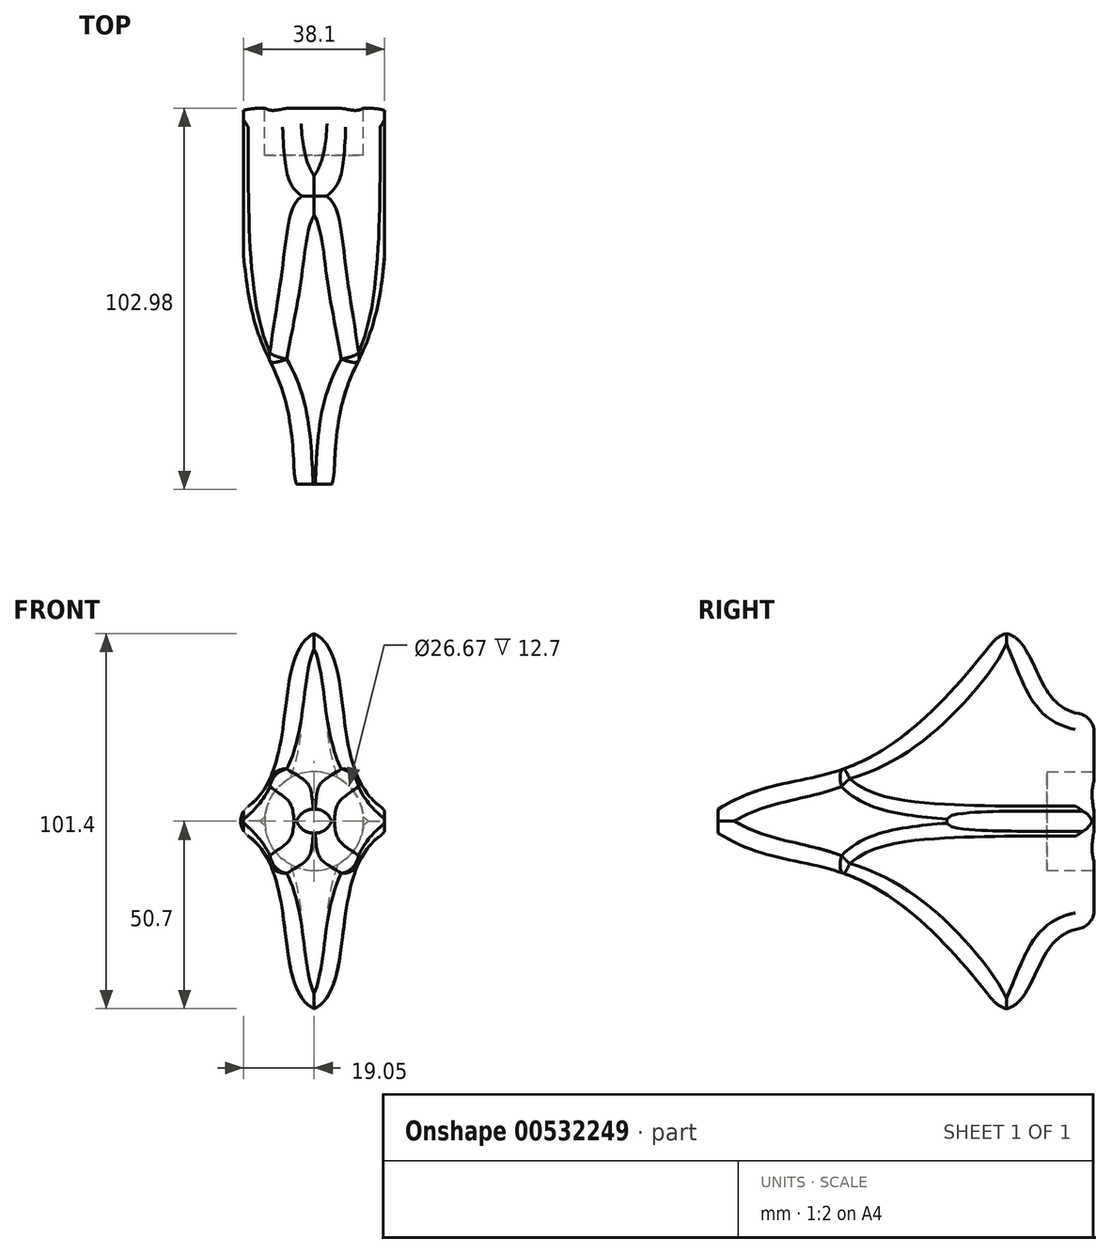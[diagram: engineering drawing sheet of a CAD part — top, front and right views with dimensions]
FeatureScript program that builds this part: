
annotation { "Feature Type Name" : "Feature", "Feature Type Description" : "" }
export const myFeature = defineFeature(function(context is Context, id is Id, definition is map)
    precondition{}
    {
        {
            var Q0;
            Q0=qCreatedBy(makeId("Front.planeOp"),FACE);
            var sketch = newSketch(context, id + "F0", { "sketchPlane" : qUnion([Q0])});
            skLineSegment(sketch, "E0.bottom", {"start": v(-16, 59.8) * mm, "end": v(22.1, 59.8) * mm});
            skLineSegment(sketch, "E0.top", {"start": v(-16, -41.8) * mm, "end": v(22.1, -41.8) * mm});
            skLineSegment(sketch, "E0.left", {"start": v(-16, 59.8) * mm, "end": v(-16, -41.8) * mm});
            skLineSegment(sketch, "E0.right", {"start": v(22.1, 59.8) * mm, "end": v(22.1, -41.8) * mm});
            skLineSegment(sketch, "E1", {"start": v(3.06, 59.8) * mm, "end": v(3.06, -41.8) * mm, "construction": true});
            skLineSegment(sketch, "E2", {"start": v(22.1, 9) * mm, "end": v(-16, 9) * mm, "construction": true});
            skFitSpline(sketch, "E3", {"points": [v(3.06, 59.8) * mm, v(-16, 12.22) * mm], "startDerivative": vector(-36.11, -18.07) * mm, "endDerivative": vector(-47.97, -28.44) * mm});
            skFitSpline(sketch, "E4.MirrorCS", {"points": [v(3.06, 59.8) * mm, v(22.1, 12.22) * mm], "startDerivative": vector(36.11, -18.07) * mm, "endDerivative": vector(47.97, -28.44) * mm});
            skFitSpline(sketch, "E5.MirrorCS", {"points": [v(3.06, -41.8) * mm, v(22.1, 5.78) * mm], "startDerivative": vector(36.11, 18.07) * mm, "endDerivative": vector(47.97, 28.44) * mm});
            skFitSpline(sketch, "E6.MirrorCS", {"points": [v(3.06, -41.8) * mm, v(-16, 5.78) * mm], "startDerivative": vector(-36.11, 18.07) * mm, "endDerivative": vector(-47.97, 28.44) * mm});
            skCircle(sketch, "E7", {"center": v(3.06, 9) * mm, "radius": 13.34 * mm});
            skSolve(sketch);
        }
        {
            var Q0;
            {var subQ3=sQuery(id+"F0.wireOp",EDGE,"E3");Q0=makeQuery(id+"F0.imprint","IMPRINT",FACE,{"disambiguationData":[TD([[makeQuery(id+"F0.imprint","IMPRINT",EDGE,{"derivedFrom":subQ3}),1.0]])]});}
            var Q1;
            Q1=makeQuery(id+"F0.imprint","IMPRINT",FACE,{"disambiguationData":[TD([[makeQuery(id+"F0.imprint","IMPRINT",EDGE,{"derivedFrom":sQuery(id+"F0.wireOp",EDGE,"kdTat6LL-pgFr-9cCU-HG4Y-xFUNoQWsQAuV")}),1.0]])]});
            var Q2;
            Q2=makeQuery(id+"F0.imprint","IMPRINT",FACE,{"disambiguationData":[TD([[makeQuery(id+"F0.imprint","IMPRINT",EDGE,{"derivedFrom":sQuery(id+"F0.wireOp",EDGE,"E7")}),1.0]])]});
            extrude(context, id + "F1", {"entities" : qUnion([Q0, Q1, Q2]), "depth" : 101.6 * mm, "offsetDistance" : 25.4 * mm});
        }
        {
            var Q0;
            Q0=makeQuery(id+"F0.imprint","IMPRINT",FACE,{"disambiguationData":[TD([[makeQuery(id+"F0.imprint","IMPRINT",EDGE,{"derivedFrom":sQuery(id+"F0.wireOp",EDGE,"E7")}),1.0]])]});
            extrude(context, id + "F2", {"entities" : qUnion([Q0]), "operationType" : NewBodyOperationType.REMOVE, "depth" : 12.7 * mm, "offsetDistance" : 25.4 * mm});
        }
        {
            var Q0;
            Q0=makeQuery(id+"F1.opExtrude","SWEPT_FACE",FACE,{"disambiguationData":[OSD([sQuery(id+"F0.wireOp",EDGE,"E0.left")])]});
            var sketch = newSketch(context, id + "F3", { "sketchPlane" : qUnion([Q0])});
            skFitSpline(sketch, "E8", {"points": [v(101.6, 12.22) * mm, v(24.43, 61.45) * mm], "startDerivative": vector(-72.72, 45.7) * mm, "endDerivative": vector(-116.16, 157.36) * mm});
            skLineSegment(sketch, "E9", {"start": v(101.6, 9) * mm, "end": v(0, 9) * mm, "construction": true});
            skFitSpline(sketch, "E10.MirrorCS", {"points": [v(101.6, 5.78) * mm, v(24.43, -43.45) * mm], "startDerivative": vector(-72.72, -45.7) * mm, "endDerivative": vector(-116.16, -157.36) * mm});
            skLineSegment(sketch, "E11", {"start": v(24.43, 61.45) * mm, "end": v(105.94, 61.45) * mm});
            skLineSegment(sketch, "E12", {"start": v(105.94, 61.45) * mm, "end": v(101.6, 12.22) * mm});
            skLineSegment(sketch, "E13.MirrorCS", {"start": v(24.43, -43.45) * mm, "end": v(105.94, -43.45) * mm});
            skLineSegment(sketch, "E14.MirrorCS", {"start": v(105.94, -43.45) * mm, "end": v(101.6, 5.78) * mm});
            skFitSpline(sketch, "E15", {"points": [v(24.43, 61.45) * mm, v(-2.72, 38.08) * mm], "startDerivative": vector(-35.2, -20.24) * mm, "endDerivative": vector(-59.28, 8.68) * mm});
            skLineSegment(sketch, "E16", {"start": v(24.43, 61.45) * mm, "end": v(-20.32, 72.54) * mm});
            skLineSegment(sketch, "E17", {"start": v(-20.32, 72.54) * mm, "end": v(-2.72, 38.08) * mm});
            skLineSegment(sketch, "E18.MirrorCS", {"start": v(-20.32, -54.54) * mm, "end": v(-2.72, -20.08) * mm});
            skFitSpline(sketch, "E19.MirrorCS", {"points": [v(24.43, -43.45) * mm, v(-2.72, -20.08) * mm], "startDerivative": vector(-35.2, 20.24) * mm, "endDerivative": vector(-59.28, -8.68) * mm});
            skLineSegment(sketch, "E20.MirrorCS", {"start": v(24.43, -43.45) * mm, "end": v(-20.32, -54.54) * mm});
            skSolve(sketch);
        }
        {
            var Q0;
            Q0=makeQuery(id+"F3.imprint","IMPRINT",FACE,{"disambiguationData":[TD([[makeQuery(id+"F3.imprint","IMPRINT",EDGE,{"derivedFrom":sQuery(id+"F3.wireOp",EDGE,"E8")}),-1.0]])]});
            var Q1;
            Q1=makeQuery(id+"F3.imprint","IMPRINT",FACE,{"disambiguationData":[TD([[makeQuery(id+"F3.imprint","IMPRINT",EDGE,{"derivedFrom":sQuery(id+"F3.wireOp",EDGE,"E10.MirrorCS")}),1.0]])]});
            extrude(context, id + "F4", {"entities" : qUnion([Q0, Q1]), "operationType" : NewBodyOperationType.REMOVE, "oppositeDirection" : true, "depth" : 762 * mm, "offsetDistance" : 25.4 * mm});
        }
        {
            var Q0;
            Q0=qCreatedBy(makeId("Top.planeOp"),FACE);
            var sketch = newSketch(context, id + "F5", { "sketchPlane" : qUnion([Q0])});
            skLineSegment(sketch, "E21", {"start": v(3.06, -117.6) * mm, "end": v(3.06, -54.23) * mm, "construction": true});
            skLineSegment(sketch, "E22", {"start": v(-16.83, -16.27) * mm, "end": v(-16.83, -108.32) * mm});
            skLineSegment(sketch, "E23", {"start": v(-16.83, -108.32) * mm, "end": v(3.06, -101.56) * mm});
            skLineSegment(sketch, "E24.MirrorCS", {"start": v(22.95, -16.27) * mm, "end": v(22.95, -108.32) * mm});
            skLineSegment(sketch, "E25.MirrorCS", {"start": v(22.95, -108.32) * mm, "end": v(3.06, -101.56) * mm});
            skFitSpline(sketch, "E26", {"points": [v(-16.83, -16.27) * mm, v(-2.27, -103.37) * mm], "startDerivative": vector(0, -195.22) * mm, "endDerivative": vector(0.96, -140.8) * mm});
            skFitSpline(sketch, "E27.MirrorCS", {"points": [v(22.95, -16.27) * mm, v(8.39, -103.37) * mm], "startDerivative": vector(0, -195.22) * mm, "endDerivative": vector(-0.96, -140.8) * mm});
            skSolve(sketch);
        }
        {
            var Q0;
            {var subQ0=sQuery(id+"F5.wireOp",EDGE,"E22");Q0=makeQuery(id+"F5.imprint","IMPRINT",FACE,{"disambiguationData":[TD([[makeQuery(id+"F5.imprint","IMPRINT",EDGE,{"derivedFrom":subQ0}),1.0]])]});}
            var Q1;
            {var subQ0=sQuery(id+"F5.wireOp",EDGE,"E24.MirrorCS");Q1=makeQuery(id+"F5.imprint","IMPRINT",FACE,{"disambiguationData":[TD([[makeQuery(id+"F5.imprint","IMPRINT",EDGE,{"derivedFrom":subQ0}),-1.0]])]});}
            extrude(context, id + "F6", {"entities" : qUnion([Q0, Q1]), "operationType" : NewBodyOperationType.REMOVE, "endBound" : BoundingType.SYMMETRIC, "oppositeDirection" : true, "depth" : 762 * mm, "offsetDistance" : 25.4 * mm});
        }
        {
            var Q0;
            Q0=makeQuery(id+"F3.imprint","IMPRINT",FACE,{"disambiguationData":[TD([[makeQuery(id+"F3.imprint","IMPRINT",EDGE,{"derivedFrom":sQuery(id+"F3.wireOp",EDGE,"E15")}),-1.0]])]});
            var Q1;
            Q1=makeQuery(id+"F3.imprint","IMPRINT",FACE,{"disambiguationData":[TD([[makeQuery(id+"F3.imprint","IMPRINT",EDGE,{"derivedFrom":sQuery(id+"F3.wireOp",EDGE,"E18.MirrorCS")}),-1.0]])]});
            extrude(context, id + "F7", {"entities" : qUnion([Q0, Q1]), "operationType" : NewBodyOperationType.REMOVE, "oppositeDirection" : true, "depth" : 50.8 * mm, "offsetDistance" : 25.4 * mm});
        }
        {
            var Q0;
            Q0=makeQuery(id+"F6.boolean.opBoolean","INTERSECT",EDGE,{"derivedFrom":[makeQuery(id+"F4.boolean.opBoolean","COPY",FACE,{"derivedFrom":makeQuery(id+"F4.opExtrude","SWEPT_FACE",FACE,{"disambiguationData":[OSD([sQuery(id+"F3.wireOp",EDGE,"E10.MirrorCS")])]})}),makeQuery(id+"F6.opExtrude","SWEPT_FACE",FACE,{"disambiguationData":[OSD([sQuery(id+"F5.wireOp",EDGE,"E26")])]})]});
            var Q1;
            Q1=makeQuery(id+"F6.boolean.opBoolean","INTERSECT",EDGE,{"derivedFrom":[makeQuery(id+"F4.boolean.opBoolean","COPY",FACE,{"derivedFrom":makeQuery(id+"F4.opExtrude","SWEPT_FACE",FACE,{"disambiguationData":[OSD([sQuery(id+"F3.wireOp",EDGE,"E8")])]})}),makeQuery(id+"F6.opExtrude","SWEPT_FACE",FACE,{"disambiguationData":[OSD([sQuery(id+"F5.wireOp",EDGE,"E26")])]})]});
            var Q2;
            Q2=makeQuery(id+"F6.boolean.opBoolean","INTERSECT",EDGE,{"derivedFrom":[makeQuery(id+"F4.boolean.opBoolean","COPY",FACE,{"derivedFrom":makeQuery(id+"F4.opExtrude","SWEPT_FACE",FACE,{"disambiguationData":[OSD([sQuery(id+"F3.wireOp",EDGE,"E10.MirrorCS")])]})}),makeQuery(id+"F6.opExtrude","SWEPT_FACE",FACE,{"disambiguationData":[OSD([sQuery(id+"F5.wireOp",EDGE,"E27.MirrorCS")])]})]});
            var Q3;
            Q3=makeQuery(id+"F6.boolean.opBoolean","INTERSECT",EDGE,{"derivedFrom":[makeQuery(id+"F4.boolean.opBoolean","COPY",FACE,{"derivedFrom":makeQuery(id+"F4.opExtrude","SWEPT_FACE",FACE,{"disambiguationData":[OSD([sQuery(id+"F3.wireOp",EDGE,"E8")])]})}),makeQuery(id+"F6.opExtrude","SWEPT_FACE",FACE,{"disambiguationData":[OSD([sQuery(id+"F5.wireOp",EDGE,"E27.MirrorCS")])]})]});
            var Q4;
            Q4=makeQuery(id+"F4.boolean.opBoolean","INTERSECT",EDGE,{"derivedFrom":[makeQuery(id+"F1.opExtrude","SWEPT_FACE",FACE,{"disambiguationData":[OSD([sQuery(id+"F0.wireOp",EDGE,"E6.MirrorCS")])]}),makeQuery(id+"F4.opExtrude","SWEPT_FACE",FACE,{"disambiguationData":[OSD([sQuery(id+"F3.wireOp",EDGE,"E10.MirrorCS")])]})]});
            var Q5;
            Q5=makeQuery(id+"F4.boolean.opBoolean","INTERSECT",EDGE,{"derivedFrom":[makeQuery(id+"F1.opExtrude","SWEPT_FACE",FACE,{"disambiguationData":[OSD([sQuery(id+"F0.wireOp",EDGE,"E5.MirrorCS")])]}),makeQuery(id+"F4.opExtrude","SWEPT_FACE",FACE,{"disambiguationData":[OSD([sQuery(id+"F3.wireOp",EDGE,"E10.MirrorCS")])]})]});
            var Q6;
            Q6=makeQuery(id+"F6.boolean.opBoolean","INTERSECT",EDGE,{"derivedFrom":[makeQuery(id+"F1.opExtrude","SWEPT_FACE",FACE,{"disambiguationData":[OSD([sQuery(id+"F0.wireOp",EDGE,"E5.MirrorCS")])]}),makeQuery(id+"F6.opExtrude","SWEPT_FACE",FACE,{"disambiguationData":[OSD([sQuery(id+"F5.wireOp",EDGE,"E27.MirrorCS")])]})]});
            var Q7;
            Q7=makeQuery(id+"F6.boolean.opBoolean","INTERSECT",EDGE,{"derivedFrom":[makeQuery(id+"F1.opExtrude","SWEPT_FACE",FACE,{"disambiguationData":[OSD([sQuery(id+"F0.wireOp",EDGE,"E4.MirrorCS")])]}),makeQuery(id+"F6.opExtrude","SWEPT_FACE",FACE,{"disambiguationData":[OSD([sQuery(id+"F5.wireOp",EDGE,"E27.MirrorCS")])]})]});
            var Q8;
            Q8=makeQuery(id+"F4.boolean.opBoolean","INTERSECT",EDGE,{"derivedFrom":[makeQuery(id+"F1.opExtrude","SWEPT_FACE",FACE,{"disambiguationData":[OSD([sQuery(id+"F0.wireOp",EDGE,"E4.MirrorCS")])]}),makeQuery(id+"F4.opExtrude","SWEPT_FACE",FACE,{"disambiguationData":[OSD([sQuery(id+"F3.wireOp",EDGE,"E8")])]})]});
            var Q9;
            Q9=makeQuery(id+"F4.boolean.opBoolean","INTERSECT",EDGE,{"derivedFrom":[makeQuery(id+"F1.opExtrude","SWEPT_FACE",FACE,{"disambiguationData":[OSD([sQuery(id+"F0.wireOp",EDGE,"E3")])]}),makeQuery(id+"F4.opExtrude","SWEPT_FACE",FACE,{"disambiguationData":[OSD([sQuery(id+"F3.wireOp",EDGE,"E8")])]})]});
            var Q10;
            Q10=makeQuery(id+"F6.boolean.opBoolean","INTERSECT",EDGE,{"derivedFrom":[makeQuery(id+"F1.opExtrude","SWEPT_FACE",FACE,{"disambiguationData":[OSD([sQuery(id+"F0.wireOp",EDGE,"E3")])]}),makeQuery(id+"F6.opExtrude","SWEPT_FACE",FACE,{"disambiguationData":[OSD([sQuery(id+"F5.wireOp",EDGE,"E26")])]})]});
            var Q11;
            Q11=makeQuery(id+"F6.boolean.opBoolean","INTERSECT",EDGE,{"derivedFrom":[makeQuery(id+"F1.opExtrude","SWEPT_FACE",FACE,{"disambiguationData":[OSD([sQuery(id+"F0.wireOp",EDGE,"E6.MirrorCS")])]}),makeQuery(id+"F6.opExtrude","SWEPT_FACE",FACE,{"disambiguationData":[OSD([sQuery(id+"F5.wireOp",EDGE,"E26")])]})]});
            fillet(context, id + "F8", {"entities" : qUnion([Q0, Q1, Q2, Q3, Q4, Q5, Q6, Q7, Q8, Q9, Q10, Q11]), "radius" : 5.08 * mm, "tangentPropagation" : true, "allowEdgeOverflow" : false});
        }
        {
            var Q0;
            Q0=makeQuery(id+"F7.boolean.opBoolean","INTERSECT",EDGE,{"derivedFrom":[makeQuery(id+"F1.opExtrude","SWEPT_FACE",FACE,{"disambiguationData":[OSD([sQuery(id+"F0.wireOp",EDGE,"E3")])]}),makeQuery(id+"F7.opExtrude","SWEPT_FACE",FACE,{"disambiguationData":[OSD([sQuery(id+"F3.wireOp",EDGE,"E15")])]})]});
            var Q1;
            Q1=makeQuery(id+"F7.boolean.opBoolean","INTERSECT",EDGE,{"derivedFrom":[makeQuery(id+"F1.opExtrude","SWEPT_FACE",FACE,{"disambiguationData":[OSD([sQuery(id+"F0.wireOp",EDGE,"E4.MirrorCS")])]}),makeQuery(id+"F7.opExtrude","SWEPT_FACE",FACE,{"disambiguationData":[OSD([sQuery(id+"F3.wireOp",EDGE,"E15")])]})]});
            var Q2;
            Q2=makeQuery(id+"F7.boolean.opBoolean","INTERSECT",EDGE,{"derivedFrom":[makeQuery(id+"F1.opExtrude","SWEPT_FACE",FACE,{"disambiguationData":[OSD([sQuery(id+"F0.wireOp",EDGE,"E6.MirrorCS")])]}),makeQuery(id+"F7.opExtrude","SWEPT_FACE",FACE,{"disambiguationData":[OSD([sQuery(id+"F3.wireOp",EDGE,"E19.MirrorCS")])]})]});
            var Q3;
            Q3=makeQuery(id+"F7.boolean.opBoolean","INTERSECT",EDGE,{"derivedFrom":[makeQuery(id+"F1.opExtrude","SWEPT_FACE",FACE,{"disambiguationData":[OSD([sQuery(id+"F0.wireOp",EDGE,"E5.MirrorCS")])]}),makeQuery(id+"F7.opExtrude","SWEPT_FACE",FACE,{"disambiguationData":[OSD([sQuery(id+"F3.wireOp",EDGE,"E19.MirrorCS")])]})]});
            var Q4;
            Q4=makeQuery(id+"F1.opExtrude","CAP_EDGE",EDGE,{"disambiguationData":[OSD([sQuery(id+"F0.wireOp",EDGE,"E6.MirrorCS")])],"isStart":true});
            var Q5;
            Q5=makeQuery(id+"F1.opExtrude","CAP_EDGE",EDGE,{"disambiguationData":[OSD([sQuery(id+"F0.wireOp",EDGE,"E5.MirrorCS")])],"isStart":true});
            var Q6;
            Q6=makeQuery(id+"F1.opExtrude","CAP_EDGE",EDGE,{"disambiguationData":[OSD([sQuery(id+"F0.wireOp",EDGE,"E4.MirrorCS")])],"isStart":true});
            var Q7;
            Q7=makeQuery(id+"F1.opExtrude","CAP_EDGE",EDGE,{"disambiguationData":[OSD([sQuery(id+"F0.wireOp",EDGE,"E3")])],"isStart":true});
            var Q8;
            {var subQ0=sQuery(id+"F0.wireOp",EDGE,"E3");var subQ1=sQuery(id+"F0.wireOp",EDGE,"E0.right");var subQ2=sQuery(id+"F0.wireOp",EDGE,"E4.MirrorCS");var subQ3=sQuery(id+"F0.wireOp",EDGE,"E0.left");var subQ4=sQuery(id+"F0.wireOp",EDGE,"E5.MirrorCS");var subQ5=sQuery(id+"F0.wireOp",EDGE,"E6.MirrorCS");Q8=makeQuery(id+"F7.boolean.opBoolean","INTERSECT",EDGE,{"derivedFrom":[makeQuery(id+"F2.boolean.opBoolean","SPLIT",FACE,{"disambiguationData":[TD([makeQuery(id+"F1.opExtrude","SWEPT_FACE",FACE,{"disambiguationData":[OSD([subQ3])]})])],"derivedFrom":makeQuery(id+"F1.opExtrude","CAP_FACE",FACE,{"disambiguationData":[OSD([subQ3,subQ1,subQ0,subQ2,subQ4,subQ5])],"isStart":true})}),makeQuery(id+"F7.opExtrude","SWEPT_FACE",FACE,{"disambiguationData":[OSD([sQuery(id+"F3.wireOp",EDGE,"E15")])]})]});}
            var Q9;
            {var subQ0=sQuery(id+"F0.wireOp",EDGE,"E3");var subQ1=sQuery(id+"F0.wireOp",EDGE,"E0.right");var subQ2=sQuery(id+"F0.wireOp",EDGE,"E4.MirrorCS");var subQ3=sQuery(id+"F0.wireOp",EDGE,"E0.left");var subQ4=sQuery(id+"F0.wireOp",EDGE,"E5.MirrorCS");var subQ5=sQuery(id+"F0.wireOp",EDGE,"E6.MirrorCS");Q9=makeQuery(id+"F7.boolean.opBoolean","INTERSECT",EDGE,{"derivedFrom":[makeQuery(id+"F2.boolean.opBoolean","SPLIT",FACE,{"disambiguationData":[TD([makeQuery(id+"F1.opExtrude","SWEPT_FACE",FACE,{"disambiguationData":[OSD([subQ3])]})])],"derivedFrom":makeQuery(id+"F1.opExtrude","CAP_FACE",FACE,{"disambiguationData":[OSD([subQ3,subQ1,subQ0,subQ2,subQ4,subQ5])],"isStart":true})}),makeQuery(id+"F7.opExtrude","SWEPT_FACE",FACE,{"disambiguationData":[OSD([sQuery(id+"F3.wireOp",EDGE,"E19.MirrorCS")])]})]});}
            fillet(context, id + "F9", {"entities" : qUnion([Q0, Q1, Q2, Q3, Q4, Q5, Q6, Q7, Q8, Q9]), "radius" : 5.08 * mm, "tangentPropagation" : true, "allowEdgeOverflow" : false});
        }
    });
